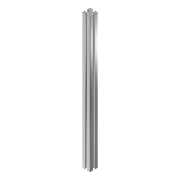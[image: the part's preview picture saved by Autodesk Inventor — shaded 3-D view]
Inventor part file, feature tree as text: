
AUTODESK INVENTOR PART (.ipt)
format: ipt  version: 2019 (Build 230136000, 136)  size: 309,760 bytes
history: native  units: mm
features: other x4, extrude x1, sketch x1, reference x1
ambient origin geometry x8: Origin, YZ Plane, XZ Plane, XY Plane, X Axis, Y Axis, Z Axis, Center Point
bodies: Body1 (feature_tree)
feature tree (7):
  other  "솔리드1"
  extrude  "돌출1"  Depth=500.0mm TaperAngle=0.0deg
  sketch  "스케치1"
  reference  "참조1"
  other  "<userpath>\Documents\Inventor\Projects\2019_CapstoneDesign\Body.iam"
  other  "Body.iam"
  other  "Propile_800:3"
